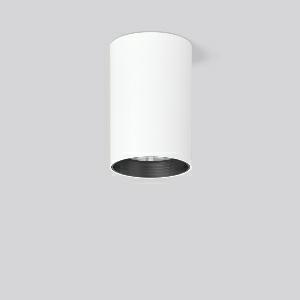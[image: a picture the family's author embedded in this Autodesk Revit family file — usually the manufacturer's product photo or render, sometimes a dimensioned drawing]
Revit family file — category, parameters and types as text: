
# Revit family: heledon_maxi_a_931221_002_3_76_629c
name_source: partatom
category: Lighting Fixtures
units: mm (PartAtom-declared; Revit-internal decimal feet)

## family parameters
Cut with Voids When Loaded = No
Host = Face
Light Source = No
Part Type = Normal
Room Calculation Point = No
Round Connector Dimension = Use Diameter
Shared = No

## types (1)
- HELEDON maxi A (1 x LED Modul 935, 2800 lm, 3500)
    Apparent Load = 25 VA
    Approval mark = CE
    CIE Flux Codes = 96 100 100 100 100
    Color Rendering = 92
    Color Temperature = 3500
    Default Elevation = 1800 mm
    Description = Series: HELEDON maxi
Cylindrical surface-mounted downlight. Housing: die-cast aluminium, powder-coated. Internal ceiling frame polycarbonate with bayonet mounting. Black plastic ring and recessed LED to prevent glare from the side. Optical assembly with lens made of plastic (polycarbonate) for the best homogeneous light distribution - can be changed without tools. Best colour rendering index Ra>90. Suitable for Ceiling mounting. Easy installation with a separate ceiling frame with bayonet mounting and plug connection. Driver integrated. Connected via plug-in connector. High quality converter without flickering and stroboscopic effect. The following accessories can be mounted without use of tools: interchangeable lenses, decorative glasses, honeycomb louvre, clear and frosted diffusers, white interchangeable plastic ring. 
Colour: traffic white, matt (RAL 9016)
Diameter: 123 mm
Height: 183 mm
Lamp: LED
Socket: without socket
Colour temperature: 3500K
Colour rendering index (CRI): 92
System power: 25 W
Rated luminous flux: 2800 lm
Luminous efficiency: 112 lm/W
Control gear: Converter, dimmable, DALI
Protection class: I
Type of protection: IP 20
    Height = 183 mm
    Lamp = 1 x LED Modul 935
    Lamp Light Flux = 2800 lm
    Lamp count = 1
    Length = 123 mm
    Lifetime = 50000 h
    Luminous efficacy = 112 lm/W
    Manufacturer = RZB
    ModVariant = No
    Model = 931221.002.3.76
    Mounting Place = Ceiling
    Mounting Type = Surface mounted
    Number of Poles = 1
    OnlyDefault = Yes
    Power Factor = 1
    Product Name = HELEDON maxi A
    Product group = Surface mounted downlights
    ProductGroupID = 302
    Protection Class = Protection class I
    Protection Degree = IP 20
    RLX_Detail_Level = 1
    RLX_Emergency_Light_Flux = 0 lm
    RLX_Emergency_Type = 0
    RLX_Emergency_Type_DB = No
    RlxData = <blob elided: 95589 chars, md5=d7155575>
    Socket = socket
    Standby Power = 0 W
    System Light Flux = 2800 lm
    System Power = 25 W
    Type Comments = Product without accessories
    Type Image = 931193.002.jpg
    URL = http://relux.com
    VarID = ---
    Voltage = 230 V
    Voltage Range = 220-240 V
    Weight = 0.00 kg
    Width = 0 mm  [stored 0 ft]

note: [stored X ft] marks values corroborated as IEEE doubles in the binary element streams (Revit-internal decimal feet)

## geometry (parser evidence)
native form markers: Blend x4, Sweep x10
no freeform markers — native parametric forms only
